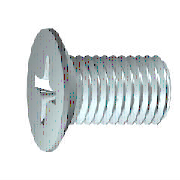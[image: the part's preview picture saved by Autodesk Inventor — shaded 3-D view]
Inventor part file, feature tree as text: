
AUTODESK INVENTOR PART (.ipt)
format: ipt  version: 2013 (Build 170138000, 138)  size: 231,936 bytes
history: native  units: mm (DEFAULTED — no unit token found)
features: sketch x1, extrude x1, plane x1
ambient origin geometry x7: Origin, YZ Plane, XZ Plane, X Axis, Y Axis, Z Axis, Center Point
bodies: Solid1 (feature_tree), Body (feature_tree)
feature tree (3):
  sketch  "Sketch1"  dims[d0=6.35mm d1=1.0922mm d2=2.5146mm d3=4.2418mm d8=90.0deg d4=1.6002mm d5=2.5908mm d6=4.625123mm d7=10.821041mm d9=3.934905mm d10=0.0mm d11=0.314849mm d12=0.314849mm d13=8.726646mm d14=1.0922mm d15=6.35mm d45=1.6002mm d16=0.0mm d17=2.5908mm d18=45.0deg d19=0.8636mm d20=1.2954mm d21=2.5908mm d22=0.1778mm d24=0.0mm d25=0.07112mm d62=45.0deg d65=0.0mm d66=0.0mm]
  extrude  "Slot"  Depth=4.2418mm
  plane  "Work Plane2"
